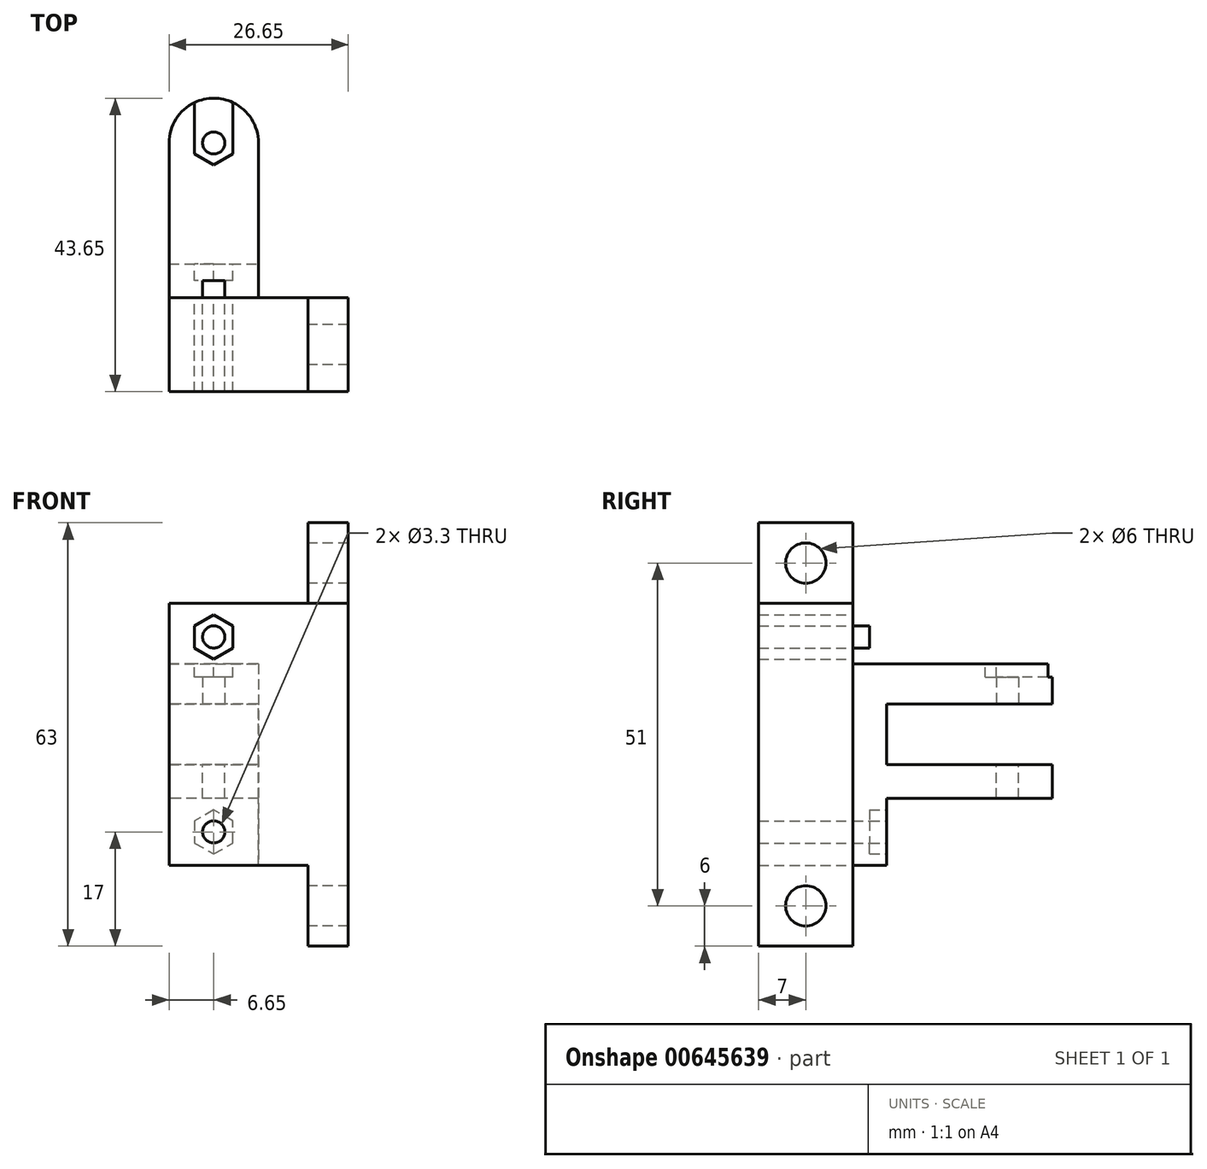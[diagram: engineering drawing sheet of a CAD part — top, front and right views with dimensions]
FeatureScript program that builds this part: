
annotation { "Feature Type Name" : "Feature", "Feature Type Description" : "" }
export const myFeature = defineFeature(function(context is Context, id is Id, definition is map)
    precondition{}
    {
        {
            var Q0;
            Q0=qCreatedBy(makeId("Top.planeOp"),FACE);
            var sketch = newSketch(context, id + "F0", { "sketchPlane" : qUnion([Q0])});
            skCircle(sketch, "E0", {"center": v(0, 0) * mm, "radius": 1.65 * mm});
            skArc(sketch, "E1.0", {"start": v(6.65, 0) * mm, "mid": v(0, 6.65) * mm, "end": v(-6.65, 0) * mm});
            skLineSegment(sketch, "E2", {"start": v(-6.65, 0) * mm, "end": v(-6.65, -23) * mm});
            skLineSegment(sketch, "E3", {"start": v(6.65, 0) * mm, "end": v(6.65, -23) * mm});
            skLineSegment(sketch, "E4", {"start": v(6.65, -23) * mm, "end": v(-6.65, -23) * mm});
            skLineSegment(sketch, "E5.bottom", {"start": v(-6.65, -23) * mm, "end": v(6.65, -23) * mm});
            skLineSegment(sketch, "E5.top", {"start": v(-6.65, -18) * mm, "end": v(6.65, -18) * mm});
            skLineSegment(sketch, "E5.left", {"start": v(-6.65, -23) * mm, "end": v(-6.65, -18) * mm});
            skLineSegment(sketch, "E5.right", {"start": v(6.65, -23) * mm, "end": v(6.65, -18) * mm});
            skSolve(sketch);
        }
        {
            var Q0;
            {var subQ7=sQuery(id+"F0.wireOp",EDGE,"E4");Q0=qUnion([makeQuery(id+"F0.imprint","IMPRINT",FACE,{"disambiguationData":[TD([[makeQuery(id+"F0.imprint","IMPRINT",EDGE,{"derivedFrom":subQ7}),-1.0]])]}),makeQuery(id+"F0.imprint","IMPRINT",FACE,{"disambiguationData":[TD([[makeQuery(id+"F0.imprint","IMPRINT",EDGE,{"derivedFrom":sQuery(id+"F0.wireOp",EDGE,"E0")}),-1.0]])]})]);}
            extrude(context, id + "F1", {"entities" : qUnion([Q0]), "depth" : 5 * mm, "offsetDistance" : 25 * mm});
        }
        {
            var Q0;
            {var subQ0=sQuery(id+"F0.wireOp",EDGE,"E4");Q0=makeQuery(id+"F0.imprint","IMPRINT",FACE,{"disambiguationData":[TD([[makeQuery(id+"F0.imprint","IMPRINT",EDGE,{"derivedFrom":subQ0}),-1.0]])]});}
            extrude(context, id + "F2", {"entities" : qUnion([Q0]), "operationType" : NewBodyOperationType.ADD, "depth" : 15 * mm, "offsetDistance" : 25 * mm});
        }
        {
            var Q0;
            {var subQ0=sQuery(id+"F0.wireOp",EDGE,"E4");Q0=makeQuery(id+"F0.imprint","IMPRINT",FACE,{"disambiguationData":[TD([[makeQuery(id+"F0.imprint","IMPRINT",EDGE,{"derivedFrom":subQ0}),-1.0]])]});}
            extrude(context, id + "F3", {"entities" : qUnion([Q0]), "operationType" : NewBodyOperationType.ADD, "oppositeDirection" : true, "depth" : 4.5 * mm, "offsetDistance" : 25 * mm});
        }
        {
            var Q0;
            Q0=makeQuery(id+"F3.opExtrude","CAP_FACE",FACE,{"disambiguationData":[OSD([sQuery(id+"F0.wireOp",EDGE,"E2"),sQuery(id+"F0.wireOp",EDGE,"E3"),sQuery(id+"F0.wireOp",EDGE,"E4"),sQuery(id+"F0.wireOp",EDGE,"E5.top")])],"isStart":false});
            cPlane(context, id + "F4", {"entities" : qUnion([Q0]), "cplaneType" : CPlaneType.OFFSET, "offset" : 0 * mm, "width" : 150 * mm, "height" : 150 * mm});
        }
        {
            var Q0;
            Q0=makeQuery(id+"F1.opExtrude","SWEPT_BODY",BODY,{"disambiguationData":[OSD([sQuery(id+"F0.wireOp",EDGE,"E0"),sQuery(id+"F0.wireOp",EDGE,"E1.0"),sQuery(id+"F0.wireOp",EDGE,"E2"),sQuery(id+"F0.wireOp",EDGE,"E3"),sQuery(id+"F0.wireOp",EDGE,"E4")])]});
            var Q1;
            Q1=qCreatedBy(id+"F4.planeOp",FACE);
            mirror(context, id + "F5", {"operationType" : NewBodyOperationType.ADD, "entities" : qUnion([Q0]), "mirrorPlane" : qUnion([Q1])});
        }
        {
            var Q0;
            Q0=makeQuery(id+"F5.opPattern","COPY",FACE,{"derivedFrom":makeQuery(id+"F2.opExtrude","SWEPT_FACE",FACE,{"disambiguationData":[OSD([sQuery(id+"F0.wireOp",EDGE,"E5.top")])]}),"instanceName":"1"});
            var sketch = newSketch(context, id + "F6", { "sketchPlane" : qUnion([Q0])});
            skCircle(sketch, "E6.cCircle", {"center": v(0, -19) * mm, "radius": 2.85 * mm, "construction": true});
            skPoint(sketch, "E6.cCircle.centerSnap0", {"position": v(0, -24) * mm});
            skLineSegment(sketch, "E6.0", {"start": v(2.85, -17.35) * mm, "end": v(2.85, -20.65) * mm});
            skLineSegment(sketch, "E6.1", {"start": v(2.85, -20.65) * mm, "end": v(0, -22.3) * mm});
            skLineSegment(sketch, "E6.2", {"start": v(0, -22.3) * mm, "end": v(-2.85, -20.65) * mm});
            skLineSegment(sketch, "E6.3", {"start": v(-2.85, -20.65) * mm, "end": v(-2.85, -17.35) * mm});
            skLineSegment(sketch, "E6.4", {"start": v(-2.85, -17.35) * mm, "end": v(0, -15.7) * mm});
            skLineSegment(sketch, "E6.5", {"start": v(0, -15.7) * mm, "end": v(2.85, -17.35) * mm});
            skPoint(sketch, "E6.0.midPoint", {"position": v(2.85, -19) * mm});
            skCircle(sketch, "E7", {"center": v(0, -19) * mm, "radius": 1.65 * mm});
            skCircle(sketch, "E8.MirrorC", {"center": v(0, 10) * mm, "radius": 1.65 * mm});
            skLineSegment(sketch, "E9.MirrorCS", {"start": v(0, 6.7) * mm, "end": v(2.85, 8.35) * mm});
            skLineSegment(sketch, "E10.MirrorCS", {"start": v(-2.85, 8.35) * mm, "end": v(0, 6.7) * mm});
            skLineSegment(sketch, "E11.MirrorCS", {"start": v(-2.85, 11.65) * mm, "end": v(-2.85, 8.35) * mm});
            skLineSegment(sketch, "E12.MirrorCS", {"start": v(2.85, 8.35) * mm, "end": v(2.85, 11.65) * mm});
            skCircle(sketch, "E13.MirrorC", {"center": v(0, 10) * mm, "radius": 2.85 * mm, "construction": true});
            skPoint(sketch, "E14.MirrorP", {"position": v(2.85, 10) * mm});
            skLineSegment(sketch, "E15.MirrorCS", {"start": v(0, 13.3) * mm, "end": v(-2.85, 11.65) * mm});
            skLineSegment(sketch, "E16.MirrorCS", {"start": v(2.85, 11.65) * mm, "end": v(0, 13.3) * mm});
            skSolve(sketch);
        }
        {
            var Q0;
            Q0=makeQuery(id+"F6.imprint","IMPRINT",FACE,{"disambiguationData":[TD([[makeQuery(id+"F6.imprint","IMPRINT",EDGE,{"derivedFrom":sQuery(id+"F6.wireOp",EDGE,"E6.0")}),-1.0]])]});
            var Q1;
            Q1=makeQuery(id+"F6.imprint","IMPRINT",FACE,{"disambiguationData":[TD([[makeQuery(id+"F6.imprint","IMPRINT",EDGE,{"derivedFrom":sQuery(id+"F6.wireOp",EDGE,"E8.MirrorC")}),1.0]])]});
            extrude(context, id + "F7", {"entities" : qUnion([Q0, Q1]), "operationType" : NewBodyOperationType.REMOVE, "oppositeDirection" : true, "depth" : 2.5 * mm, "offsetDistance" : 25 * mm});
        }
        {
            var Q0;
            Q0=makeQuery(id+"F7.boolean.opBoolean","SPLIT",FACE,{"disambiguationData":[TD([makeQuery(id+"F7.opExtrude","SWEPT_FACE",FACE,{"disambiguationData":[OSD([sQuery(id+"F6.wireOp",EDGE,"E7")])]})])],"derivedFrom":makeQuery(id+"F5.opPattern","COPY",FACE,{"derivedFrom":makeQuery(id+"F2.opExtrude","SWEPT_FACE",FACE,{"disambiguationData":[OSD([sQuery(id+"F0.wireOp",EDGE,"E5.top")])]}),"instanceName":"1"})});
            var Q1;
            Q1=makeQuery(id+"F7.boolean.opBoolean","SPLIT",FACE,{"disambiguationData":[TD([makeQuery(id+"F7.opExtrude","SWEPT_FACE",FACE,{"disambiguationData":[OSD([sQuery(id+"F6.wireOp",EDGE,"E8.MirrorC")])]})])],"derivedFrom":makeQuery(id+"F2.opExtrude","SWEPT_FACE",FACE,{"disambiguationData":[OSD([sQuery(id+"F0.wireOp",EDGE,"E5.top")])]})});
            extrude(context, id + "F8", {"entities" : qUnion([Q0, Q1]), "operationType" : NewBodyOperationType.REMOVE, "oppositeDirection" : true, "depth" : 25 * mm, "offsetDistance" : 25 * mm});
        }
        {
            var Q0;
            Q0=makeQuery(id+"F1.opExtrude","CAP_FACE",FACE,{"disambiguationData":[OSD([sQuery(id+"F0.wireOp",EDGE,"E0"),sQuery(id+"F0.wireOp",EDGE,"E1.0"),sQuery(id+"F0.wireOp",EDGE,"E2"),sQuery(id+"F0.wireOp",EDGE,"E3"),sQuery(id+"F0.wireOp",EDGE,"E4")])],"isStart":false});
            var sketch = newSketch(context, id + "F9", { "sketchPlane" : qUnion([Q0])});
            skCircle(sketch, "E17.cCircle", {"center": v(0, 0) * mm, "radius": 2.85 * mm, "construction": true});
            skLineSegment(sketch, "E17.0", {"start": v(2.85, 1.65) * mm, "end": v(2.85, -1.65) * mm});
            skLineSegment(sketch, "E17.1", {"start": v(2.85, -1.65) * mm, "end": v(0, -3.3) * mm});
            skLineSegment(sketch, "E17.2", {"start": v(0, -3.3) * mm, "end": v(-2.85, -1.65) * mm});
            skLineSegment(sketch, "E17.3", {"start": v(-2.85, -1.65) * mm, "end": v(-2.85, 1.65) * mm});
            skLineSegment(sketch, "E17.4", {"start": v(-2.85, 1.65) * mm, "end": v(0, 3.3) * mm});
            skLineSegment(sketch, "E17.5", {"start": v(0, 3.3) * mm, "end": v(2.85, 1.65) * mm});
            skPoint(sketch, "E17.0.midPoint", {"position": v(2.85, 0) * mm});
            skLineSegment(sketch, "E18", {"start": v(-2.85, 1.65) * mm, "end": v(-2.85, 6) * mm});
            skLineSegment(sketch, "E19", {"start": v(2.85, 1.65) * mm, "end": v(2.85, 6) * mm});
            skSolve(sketch);
        }
        {
            var Q0;
            Q0 = qSketchRegion(id + "F9", true);
            var Q1;
            Q1=makeQuery(id+"F9.imprint","IMPRINT",FACE,{"disambiguationData":[TD([[makeQuery(id+"F9.imprint","IMPRINT",EDGE,{"derivedFrom":sQuery(id+"F9.wireOp",EDGE,"E17.4")}),1.0]])]});
            extrude(context, id + "F10", {"entities" : qUnion([Q0, Q1]), "operationType" : NewBodyOperationType.REMOVE, "oppositeDirection" : true, "depth" : 1 * mm, "offsetDistance" : 25 * mm});
        }
        {
            var Q0;
            Q0=makeQuery(id+"F1.opExtrude","CAP_FACE",FACE,{"disambiguationData":[OSD([sQuery(id+"F0.wireOp",EDGE,"E0"),sQuery(id+"F0.wireOp",EDGE,"E1.0"),sQuery(id+"F0.wireOp",EDGE,"E2"),sQuery(id+"F0.wireOp",EDGE,"E3"),sQuery(id+"F0.wireOp",EDGE,"E4")])],"isStart":false});
            extrude(context, id + "F11", {"entities" : qUnion([Q0]), "operationType" : NewBodyOperationType.ADD, "depth" : 1 * mm, "offsetDistance" : 25 * mm});
        }
        {
            var Q0;
            {var subQ0=sQuery(id+"F0.wireOp",EDGE,"E4");var subQ1=makeQuery(id+"F3.boolean.opBoolean","MERGE",FACE,{"derivedFrom":[makeQuery(id+"F2.boolean.opBoolean","MERGE",FACE,{"derivedFrom":[makeQuery(id+"F1.opExtrude","SWEPT_FACE",FACE,{"disambiguationData":[OSD([subQ0])]}),makeQuery(id+"F2.opExtrude","SWEPT_FACE",FACE,{"disambiguationData":[OSD([subQ0])]})]}),makeQuery(id+"F3.opExtrude","SWEPT_FACE",FACE,{"disambiguationData":[OSD([subQ0])]})]});Q0=makeQuery(id+"F5.boolean.opBoolean","MERGE",FACE,{"derivedFrom":[subQ1,makeQuery(id+"F5.opPattern","COPY",FACE,{"derivedFrom":subQ1,"instanceName":"1"})]});}
            var sketch = newSketch(context, id + "F12", { "sketchPlane" : qUnion([Q0])});
            skLineSegment(sketch, "E20.bottom", {"start": v(-6.65, -24) * mm, "end": v(20, -24) * mm});
            skLineSegment(sketch, "E20.top", {"start": v(-6.65, 15) * mm, "end": v(20, 15) * mm});
            skLineSegment(sketch, "E20.left", {"start": v(-6.65, -24) * mm, "end": v(-6.65, 15) * mm});
            skLineSegment(sketch, "E20.right", {"start": v(20, -24) * mm, "end": v(20, 15) * mm});
            skSolve(sketch);
        }
        {
            var Q0;
            Q0 = qSketchRegion(id + "F12", true);
            extrude(context, id + "F13", {"entities" : qUnion([Q0]), "depth" : 14 * mm, "offsetDistance" : 25 * mm});
        }
        {
            var Q0;
            Q0=makeQuery(id+"F6.imprint","IMPRINT",FACE,{"disambiguationData":[TD([[makeQuery(id+"F6.imprint","IMPRINT",EDGE,{"derivedFrom":sQuery(id+"F6.wireOp",EDGE,"E7")}),1.0]])]});
            var Q1;
            Q1=makeQuery(id+"F6.imprint","IMPRINT",FACE,{"disambiguationData":[TD([[makeQuery(id+"F6.imprint","IMPRINT",EDGE,{"derivedFrom":sQuery(id+"F6.wireOp",EDGE,"E8.MirrorC")}),-1.0]])]});
            extrude(context, id + "F14", {"entities" : qUnion([Q0, Q1]), "operationType" : NewBodyOperationType.REMOVE, "oppositeDirection" : true, "depth" : 25 * mm, "offsetDistance" : 25 * mm});
        }
        {
            var Q0;
            Q0=makeQuery(id+"F13.opExtrude","SWEPT_FACE",FACE,{"disambiguationData":[OSD([sQuery(id+"F12.wireOp",EDGE,"E20.top")])]});
            var sketch = newSketch(context, id + "F15", { "sketchPlane" : qUnion([Q0])});
            skLineSegment(sketch, "E21.bottom", {"start": v(20, -37) * mm, "end": v(14, -37) * mm});
            skLineSegment(sketch, "E21.top", {"start": v(20, -23) * mm, "end": v(14, -23) * mm});
            skLineSegment(sketch, "E21.left", {"start": v(20, -37) * mm, "end": v(20, -23) * mm});
            skLineSegment(sketch, "E21.right", {"start": v(14, -37) * mm, "end": v(14, -23) * mm});
            skSolve(sketch);
        }
        {
            var Q0;
            Q0 = qSketchRegion(id + "F15", true);
            extrude(context, id + "F16", {"entities" : qUnion([Q0]), "depth" : 12 * mm, "offsetDistance" : 25 * mm});
        }
        {
            var Q0;
            Q0=makeQuery(id+"F16.opExtrude","SWEPT_FACE",FACE,{"disambiguationData":[OSD([sQuery(id+"F15.wireOp",EDGE,"E21.right")])]});
            var sketch = newSketch(context, id + "F17", { "sketchPlane" : qUnion([Q0])});
            skCircle(sketch, "E22", {"center": v(30, 21) * mm, "radius": 3 * mm});
            skPoint(sketch, "E22.centerSnap0", {"position": v(23, 21) * mm});
            skPoint(sketch, "E22.centerSnap1", {"position": v(30, 27) * mm});
            skSolve(sketch);
        }
        {
            var Q0;
            Q0 = qSketchRegion(id + "F17", true);
            extrude(context, id + "F18", {"entities" : qUnion([Q0]), "operationType" : NewBodyOperationType.REMOVE, "oppositeDirection" : true, "depth" : 25 * mm, "offsetDistance" : 25 * mm});
        }
        {
            var Q0;
            Q0=makeQuery(id+"F13.opExtrude","SWEPT_FACE",FACE,{"disambiguationData":[OSD([sQuery(id+"F12.wireOp",EDGE,"E20.bottom")])]});
            var sketch = newSketch(context, id + "F19", { "sketchPlane" : qUnion([Q0])});
            skLineSegment(sketch, "E23.bottom", {"start": v(20, 23) * mm, "end": v(14, 23) * mm});
            skLineSegment(sketch, "E23.top", {"start": v(20, 37) * mm, "end": v(14, 37) * mm});
            skLineSegment(sketch, "E23.left", {"start": v(20, 23) * mm, "end": v(20, 37) * mm});
            skLineSegment(sketch, "E23.right", {"start": v(14, 23) * mm, "end": v(14, 37) * mm});
            skSolve(sketch);
        }
        {
            var Q0;
            Q0 = qSketchRegion(id + "F19", true);
            extrude(context, id + "F20", {"entities" : qUnion([Q0]), "operationType" : NewBodyOperationType.ADD, "depth" : 12 * mm, "offsetDistance" : 25 * mm});
        }
        {
            var Q0;
            Q0=makeQuery(id+"F20.opExtrude","SWEPT_FACE",FACE,{"disambiguationData":[OSD([sQuery(id+"F19.wireOp",EDGE,"E23.right")])]});
            var sketch = newSketch(context, id + "F21", { "sketchPlane" : qUnion([Q0])});
            skCircle(sketch, "E24", {"center": v(30, -30) * mm, "radius": 3 * mm});
            skPoint(sketch, "E24.centerSnap0", {"position": v(37, -30) * mm});
            skPoint(sketch, "E24.centerSnap1", {"position": v(30, -36) * mm});
            skSolve(sketch);
        }
        {
            var Q0;
            Q0 = qSketchRegion(id + "F21", true);
            extrude(context, id + "F22", {"entities" : qUnion([Q0]), "operationType" : NewBodyOperationType.REMOVE, "oppositeDirection" : true, "depth" : 25 * mm, "offsetDistance" : 25 * mm});
        }
    });
